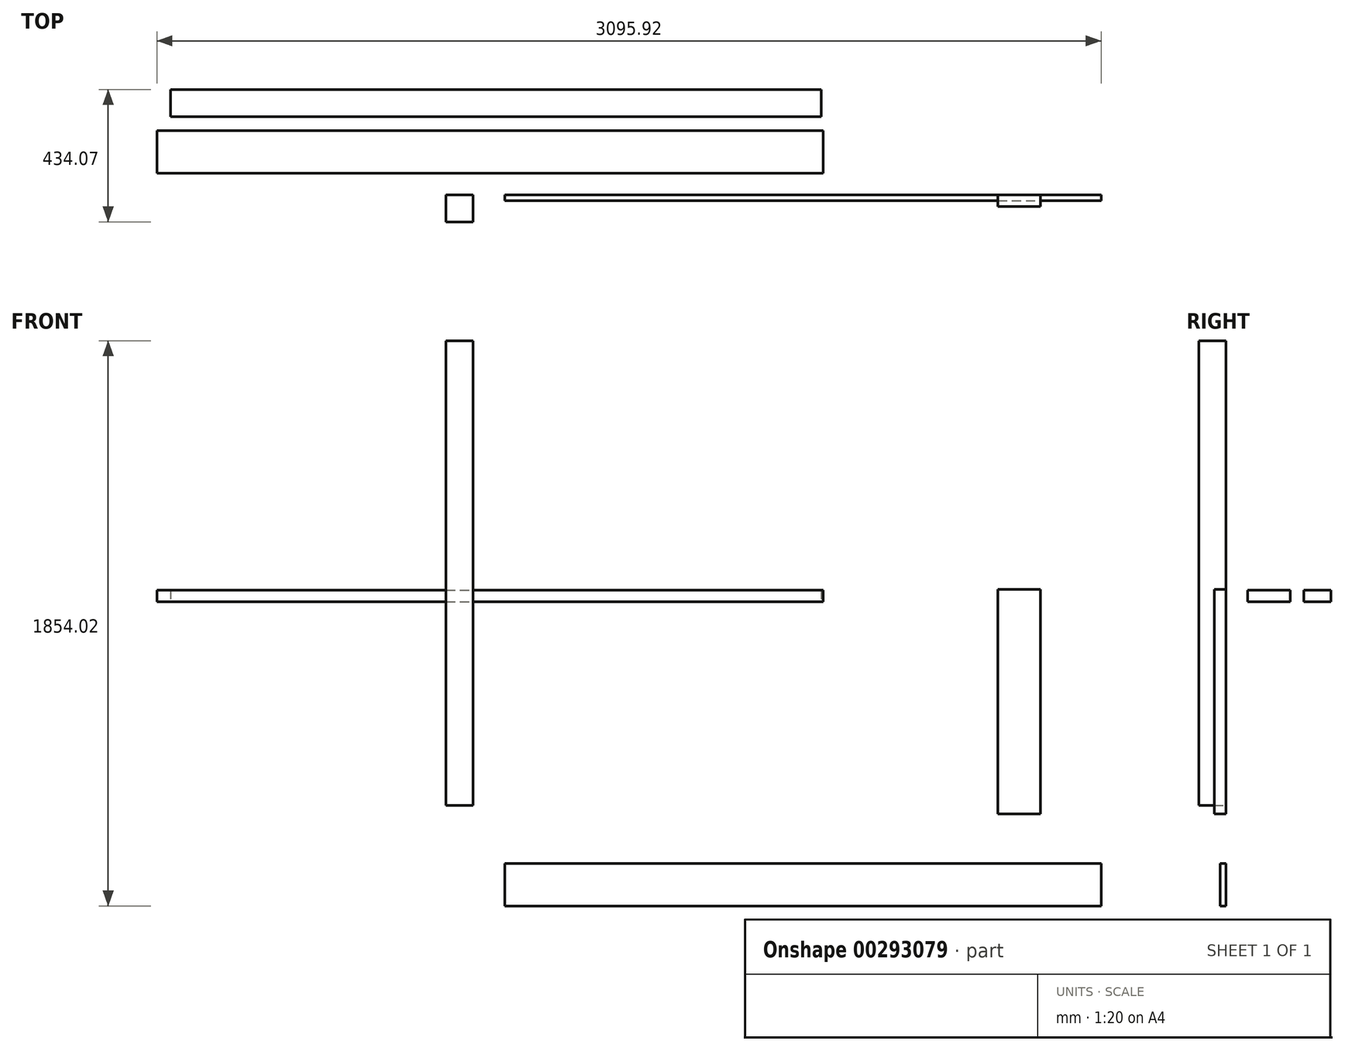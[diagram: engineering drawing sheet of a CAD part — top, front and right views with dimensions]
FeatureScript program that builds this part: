
annotation { "Feature Type Name" : "Feature", "Feature Type Description" : "" }
export const myFeature = defineFeature(function(context is Context, id is Id, definition is map)
    precondition{}
    {
        {
            var Q0;
            Q0=qCreatedBy(makeId("Front.planeOp"),FACE);
            var sketch = newSketch(context, id + "F0", { "sketchPlane" : qUnion([Q0])});
            skLineSegment(sketch, "E0.bottom", {"start": v(-1002.28, 855.85) * mm, "end": v(-913.38, 855.85) * mm});
            skLineSegment(sketch, "E0.top", {"start": v(-1002.28, -668.15) * mm, "end": v(-913.38, -668.15) * mm});
            skLineSegment(sketch, "E0.left", {"start": v(-1002.28, 855.85) * mm, "end": v(-1002.28, -668.15) * mm});
            skLineSegment(sketch, "E0.right", {"start": v(-913.38, 855.85) * mm, "end": v(-913.38, -668.15) * mm});
            skSolve(sketch);
        }
        {
            var Q0;
            Q0=makeQuery(id+"F0.imprint","IMPRINT",FACE,{"disambiguationData":[TD([[makeQuery(id+"F0.imprint","IMPRINT",EDGE,{"derivedFrom":sQuery(id+"F0.wireOp",EDGE,"E0.bottom")}),-1.0]])]});
            extrude(context, id + "F1", {"entities" : qUnion([Q0]), "depth" : 88.9 * mm});
        }
        {
            var Q0;
            Q0=qCreatedBy(makeId("Top.planeOp"),FACE);
            var sketch = newSketch(context, id + "F2", { "sketchPlane" : qUnion([Q0])});
            skLineSegment(sketch, "E1.bottom", {"start": v(-1906.07, 345.17) * mm, "end": v(227.53, 345.17) * mm});
            skLineSegment(sketch, "E1.top", {"start": v(-1906.07, 256.27) * mm, "end": v(227.53, 256.27) * mm});
            skLineSegment(sketch, "E1.left", {"start": v(-1906.07, 345.17) * mm, "end": v(-1906.07, 256.27) * mm});
            skLineSegment(sketch, "E1.right", {"start": v(227.53, 345.17) * mm, "end": v(227.53, 256.27) * mm});
            skSolve(sketch);
        }
        {
            var Q0;
            Q0=makeQuery(id+"F2.imprint","IMPRINT",FACE,{"disambiguationData":[TD([[makeQuery(id+"F2.imprint","IMPRINT",EDGE,{"derivedFrom":sQuery(id+"F2.wireOp",EDGE,"E1.bottom")}),-1.0]])]});
            extrude(context, id + "F3", {"entities" : qUnion([Q0]), "depth" : 38.1 * mm});
        }
        {
            var Q0;
            Q0=qCreatedBy(makeId("Top.planeOp"),FACE);
            var sketch = newSketch(context, id + "F4", { "sketchPlane" : qUnion([Q0])});
            skLineSegment(sketch, "E2.bottom", {"start": v(-1950.08, 210.74) * mm, "end": v(234.32, 210.74) * mm});
            skLineSegment(sketch, "E2.top", {"start": v(-1950.08, 71.04) * mm, "end": v(234.32, 71.04) * mm});
            skLineSegment(sketch, "E2.left", {"start": v(-1950.08, 210.74) * mm, "end": v(-1950.08, 71.04) * mm});
            skLineSegment(sketch, "E2.right", {"start": v(234.32, 210.74) * mm, "end": v(234.32, 71.04) * mm});
            skSolve(sketch);
        }
        {
            var Q0;
            Q0=makeQuery(id+"F4.imprint","IMPRINT",FACE,{"disambiguationData":[TD([[makeQuery(id+"F4.imprint","IMPRINT",EDGE,{"derivedFrom":sQuery(id+"F4.wireOp",EDGE,"E2.bottom")}),-1.0]])]});
            extrude(context, id + "F5", {"entities" : qUnion([Q0]), "depth" : 38.1 * mm});
        }
        {
            var Q0;
            Q0=qCreatedBy(makeId("Front.planeOp"),FACE);
            var sketch = newSketch(context, id + "F6", { "sketchPlane" : qUnion([Q0])});
            skLineSegment(sketch, "E3.bottom", {"start": v(-809.96, -858.47) * mm, "end": v(1145.84, -858.47) * mm});
            skLineSegment(sketch, "E3.top", {"start": v(-809.96, -998.17) * mm, "end": v(1145.84, -998.17) * mm});
            skLineSegment(sketch, "E3.left", {"start": v(-809.96, -858.47) * mm, "end": v(-809.96, -998.17) * mm});
            skLineSegment(sketch, "E3.right", {"start": v(1145.84, -858.47) * mm, "end": v(1145.84, -998.17) * mm});
            skSolve(sketch);
        }
        {
            var Q0;
            Q0=makeQuery(id+"F6.imprint","IMPRINT",FACE,{"disambiguationData":[TD([[makeQuery(id+"F6.imprint","IMPRINT",EDGE,{"derivedFrom":sQuery(id+"F6.wireOp",EDGE,"E3.bottom")}),-1.0]])]});
            extrude(context, id + "F7", {"entities" : qUnion([Q0]), "depth" : 19.05 * mm});
        }
        {
            var Q0;
            Q0=qCreatedBy(makeId("Front.planeOp"),FACE);
            var sketch = newSketch(context, id + "F8", { "sketchPlane" : qUnion([Q0])});
            skLineSegment(sketch, "E4.bottom", {"start": v(807.55, 40.5) * mm, "end": v(947.25, 40.5) * mm});
            skLineSegment(sketch, "E4.top", {"start": v(807.55, -696.1) * mm, "end": v(947.25, -696.1) * mm});
            skLineSegment(sketch, "E4.left", {"start": v(807.55, 40.5) * mm, "end": v(807.55, -696.1) * mm});
            skLineSegment(sketch, "E4.right", {"start": v(947.25, 40.5) * mm, "end": v(947.25, -696.1) * mm});
            skSolve(sketch);
        }
        {
            var Q0;
            Q0=makeQuery(id+"F8.imprint","IMPRINT",FACE,{"disambiguationData":[TD([[makeQuery(id+"F8.imprint","IMPRINT",EDGE,{"derivedFrom":sQuery(id+"F8.wireOp",EDGE,"E4.bottom")}),-1.0]])]});
            extrude(context, id + "F9", {"entities" : qUnion([Q0]), "depth" : 38.1 * mm});
        }
    });
